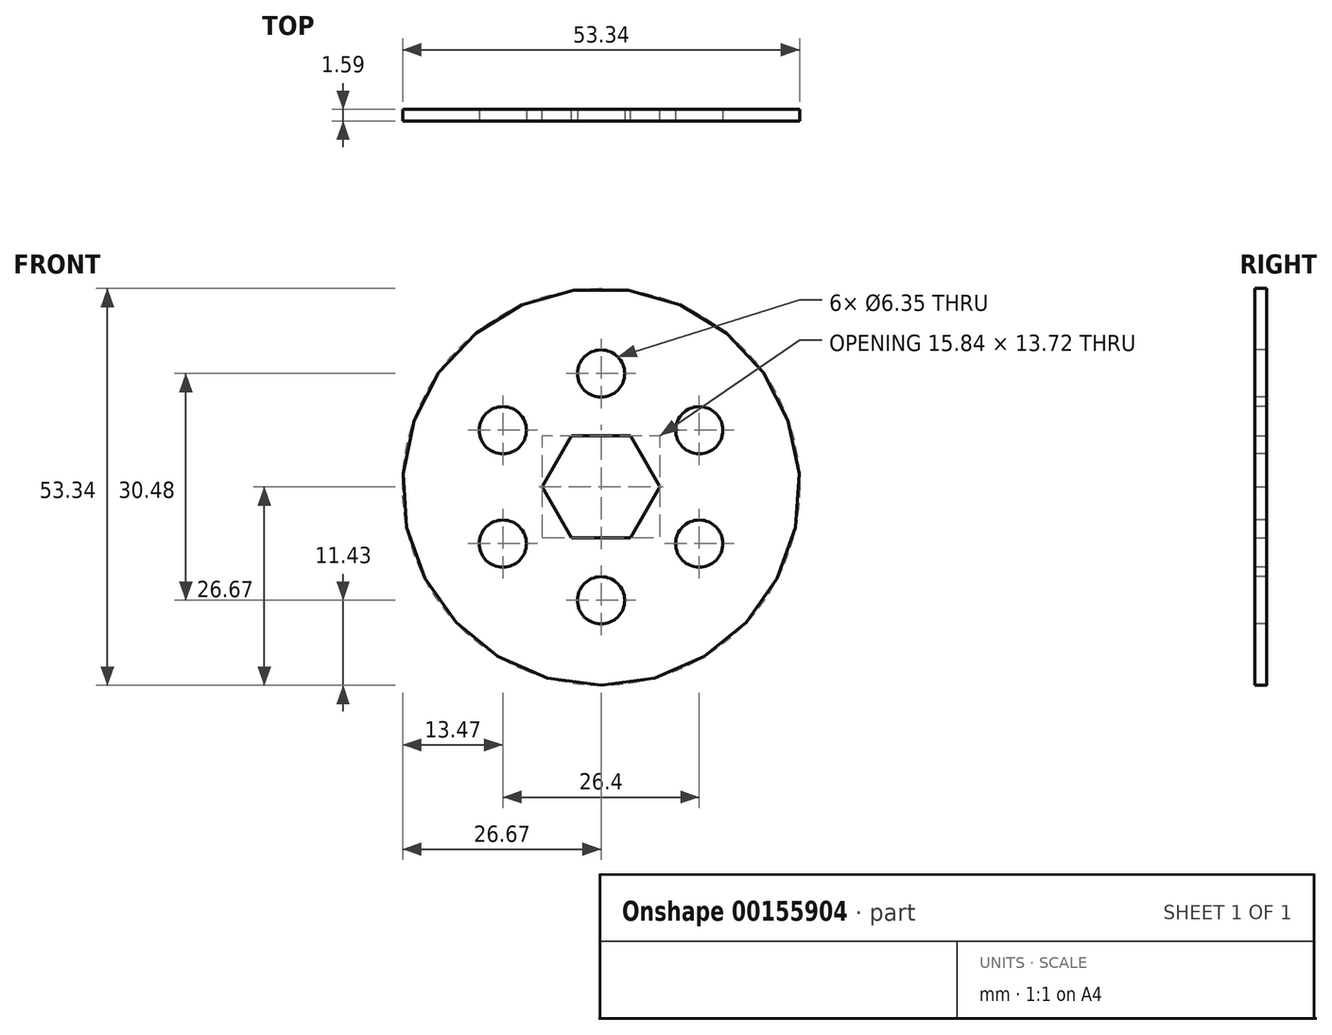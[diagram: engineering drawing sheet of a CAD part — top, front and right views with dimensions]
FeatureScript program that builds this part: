
annotation { "Feature Type Name" : "Feature", "Feature Type Description" : "" }
export const myFeature = defineFeature(function(context is Context, id is Id, definition is map)
    precondition{}
    {
        {
            var Q0;
            Q0=qCreatedBy(makeId("Front.planeOp"),FACE);
            var sketch = newSketch(context, id + "F0", { "sketchPlane" : qUnion([Q0])});
            skCircle(sketch, "E0", {"center": v(0, 0) * mm, "radius": 25.4 * mm});
            skCircle(sketch, "E1", {"center": v(0, 0) * mm, "radius": 7.92 * mm});
            skCircle(sketch, "E2", {"center": v(0, 0) * mm, "radius": 26.67 * mm});
            skCircle(sketch, "E3.cCircle", {"center": v(0, 0) * mm, "radius": 7.92 * mm, "construction": true});
            skLineSegment(sketch, "E3.0", {"start": v(3.96, 6.86) * mm, "end": v(7.92, 0) * mm});
            skLineSegment(sketch, "E3.1", {"start": v(7.92, 0) * mm, "end": v(3.96, -6.86) * mm});
            skLineSegment(sketch, "E3.2", {"start": v(3.96, -6.86) * mm, "end": v(-3.96, -6.86) * mm});
            skLineSegment(sketch, "E3.3", {"start": v(-3.96, -6.86) * mm, "end": v(-7.92, 0) * mm});
            skLineSegment(sketch, "E3.4", {"start": v(-7.92, 0) * mm, "end": v(-3.96, 6.86) * mm});
            skLineSegment(sketch, "E3.5", {"start": v(-3.96, 6.86) * mm, "end": v(3.96, 6.86) * mm});
            skSolve(sketch);
        }
        {
            var Q0;
            Q0 = qSketchRegion(id + "F0", true);
            var Q1;
            Q1=makeQuery(id+"F0.imprint","IMPRINT",FACE,{"disambiguationData":[TD([[makeQuery(id+"F0.imprint","IMPRINT",EDGE,{"derivedFrom":sQuery(id+"F0.wireOp",EDGE,"E0")}),1.0]])]});
            var Q2;
            Q2=makeQuery(id+"F0.imprint","IMPRINT",FACE,{"disambiguationData":[TD([[makeQuery(id+"F0.imprint","IMPRINT",EDGE,{"derivedFrom":sQuery(id+"F0.wireOp",EDGE,"E3.0")}),-1.0]])]});
            var Q3;
            {var subQ0=sQuery(id+"F0.wireOp",EDGE,"E3.5");Q3=makeQuery(id+"F0.imprint","IMPRINT",FACE,{"disambiguationData":[TD([[makeQuery(id+"F0.imprint","IMPRINT",EDGE,{"derivedFrom":subQ0}),1.0]])]});}
            var Q4;
            {var subQ0=sQuery(id+"F0.wireOp",EDGE,"E3.0");Q4=makeQuery(id+"F0.imprint","IMPRINT",FACE,{"disambiguationData":[TD([[makeQuery(id+"F0.imprint","IMPRINT",EDGE,{"derivedFrom":subQ0}),1.0]])]});}
            var Q5;
            {var subQ0=sQuery(id+"F0.wireOp",EDGE,"E3.1");Q5=makeQuery(id+"F0.imprint","IMPRINT",FACE,{"disambiguationData":[TD([[makeQuery(id+"F0.imprint","IMPRINT",EDGE,{"derivedFrom":subQ0}),1.0]])]});}
            var Q6;
            {var subQ0=sQuery(id+"F0.wireOp",EDGE,"E3.2");Q6=makeQuery(id+"F0.imprint","IMPRINT",FACE,{"disambiguationData":[TD([[makeQuery(id+"F0.imprint","IMPRINT",EDGE,{"derivedFrom":subQ0}),1.0]])]});}
            var Q7;
            {var subQ0=sQuery(id+"F0.wireOp",EDGE,"E3.3");Q7=makeQuery(id+"F0.imprint","IMPRINT",FACE,{"disambiguationData":[TD([[makeQuery(id+"F0.imprint","IMPRINT",EDGE,{"derivedFrom":subQ0}),1.0]])]});}
            var Q8;
            {var subQ0=sQuery(id+"F0.wireOp",EDGE,"E3.4");Q8=makeQuery(id+"F0.imprint","IMPRINT",FACE,{"disambiguationData":[TD([[makeQuery(id+"F0.imprint","IMPRINT",EDGE,{"derivedFrom":subQ0}),1.0]])]});}
            extrude(context, id + "F1", {"entities" : qUnion([Q0, Q1, Q2, Q3, Q4, Q5, Q6, Q7, Q8]), "depth" : 1 / 406.4 * mm});
        }
        {
            var Q0;
            Q0=makeQuery(id+"F1.opExtrude","CAP_FACE",FACE,{"disambiguationData":[OSD([sQuery(id+"F0.wireOp",EDGE,"E2")])],"isStart":false});
            var sketch = newSketch(context, id + "F2", { "sketchPlane" : qUnion([Q0])});
            skCircle(sketch, "E4.0", {"center": v(0, 0) * mm, "radius": 25.4 * mm});
            skCircle(sketch, "E5.0", {"center": v(0, 0) * mm, "radius": 7.92 * mm});
            skLineSegment(sketch, "E6.0", {"start": v(3.96, 6.86) * mm, "end": v(7.92, 0) * mm});
            skLineSegment(sketch, "E7.0", {"start": v(7.92, 0) * mm, "end": v(3.96, -6.86) * mm});
            skLineSegment(sketch, "E8.0", {"start": v(3.96, -6.86) * mm, "end": v(-3.96, -6.86) * mm});
            skLineSegment(sketch, "E9.0", {"start": v(-3.96, -6.86) * mm, "end": v(-7.92, 0) * mm});
            skLineSegment(sketch, "E10.0", {"start": v(-7.92, 0) * mm, "end": v(-3.96, 6.86) * mm});
            skLineSegment(sketch, "E11.0", {"start": v(-3.96, 6.86) * mm, "end": v(3.96, 6.86) * mm});
            skSolve(sketch);
        }
        {
            var Q0;
            Q0=makeQuery(id+"F2.imprint","IMPRINT",FACE,{"disambiguationData":[TD([[makeQuery(id+"F2.imprint","IMPRINT",EDGE,{"derivedFrom":sQuery(id+"F2.wireOp",EDGE,"E4.0")}),1.0]])]});
            var Q1;
            {var subQ0=sQuery(id+"F2.wireOp",EDGE,"E6.0");Q1=makeQuery(id+"F2.imprint","IMPRINT",FACE,{"disambiguationData":[TD([[makeQuery(id+"F2.imprint","IMPRINT",EDGE,{"derivedFrom":subQ0}),1.0]])]});}
            var Q2;
            {var subQ0=sQuery(id+"F2.wireOp",EDGE,"E11.0");Q2=makeQuery(id+"F2.imprint","IMPRINT",FACE,{"disambiguationData":[TD([[makeQuery(id+"F2.imprint","IMPRINT",EDGE,{"derivedFrom":subQ0}),1.0]])]});}
            var Q3;
            {var subQ0=sQuery(id+"F2.wireOp",EDGE,"E10.0");Q3=makeQuery(id+"F2.imprint","IMPRINT",FACE,{"disambiguationData":[TD([[makeQuery(id+"F2.imprint","IMPRINT",EDGE,{"derivedFrom":subQ0}),1.0]])]});}
            var Q4;
            {var subQ0=sQuery(id+"F2.wireOp",EDGE,"E9.0");Q4=makeQuery(id+"F2.imprint","IMPRINT",FACE,{"disambiguationData":[TD([[makeQuery(id+"F2.imprint","IMPRINT",EDGE,{"derivedFrom":subQ0}),1.0]])]});}
            var Q5;
            {var subQ0=sQuery(id+"F2.wireOp",EDGE,"E8.0");Q5=makeQuery(id+"F2.imprint","IMPRINT",FACE,{"disambiguationData":[TD([[makeQuery(id+"F2.imprint","IMPRINT",EDGE,{"derivedFrom":subQ0}),1.0]])]});}
            var Q6;
            {var subQ0=sQuery(id+"F2.wireOp",EDGE,"E7.0");Q6=makeQuery(id+"F2.imprint","IMPRINT",FACE,{"disambiguationData":[TD([[makeQuery(id+"F2.imprint","IMPRINT",EDGE,{"derivedFrom":subQ0}),1.0]])]});}
            extrude(context, id + "F3", {"entities" : qUnion([Q0, Q1, Q2, Q3, Q4, Q5, Q6]), "operationType" : NewBodyOperationType.ADD, "depth" : 1 / 406.4 * mm});
        }
        {
            var Q0;
            Q0=makeQuery(id+"F3.opExtrude","CAP_FACE",FACE,{"disambiguationData":[OSD([sQuery(id+"F2.wireOp",EDGE,"E4.0"),sQuery(id+"F2.wireOp",EDGE,"E6.0"),sQuery(id+"F2.wireOp",EDGE,"E7.0"),sQuery(id+"F2.wireOp",EDGE,"E8.0"),sQuery(id+"F2.wireOp",EDGE,"E9.0"),sQuery(id+"F2.wireOp",EDGE,"E10.0"),sQuery(id+"F2.wireOp",EDGE,"E11.0")])],"isStart":false});
            var sketch = newSketch(context, id + "F4", { "sketchPlane" : qUnion([Q0])});
            skCircle(sketch, "E12.0", {"center": v(0, 0) * mm, "radius": 26.67 * mm});
            skLineSegment(sketch, "E13.0", {"start": v(3.96, -6.86) * mm, "end": v(-3.96, -6.86) * mm});
            skLineSegment(sketch, "E14.0", {"start": v(7.92, 0) * mm, "end": v(3.96, -6.86) * mm});
            skLineSegment(sketch, "E15.0", {"start": v(3.96, 6.86) * mm, "end": v(7.92, 0) * mm});
            skLineSegment(sketch, "E16.0", {"start": v(-3.96, 6.86) * mm, "end": v(3.96, 6.86) * mm});
            skLineSegment(sketch, "E17.0", {"start": v(-7.92, 0) * mm, "end": v(-3.96, 6.86) * mm});
            skLineSegment(sketch, "E18.0", {"start": v(-3.96, -6.86) * mm, "end": v(-7.92, 0) * mm});
            skSolve(sketch);
        }
        {
            var Q0;
            Q0=makeQuery(id+"F4.imprint","IMPRINT",FACE,{"disambiguationData":[TD([[makeQuery(id+"F4.imprint","IMPRINT",EDGE,{"derivedFrom":sQuery(id+"F4.wireOp",EDGE,"E13.0")}),1.0]])]});
            var Q1;
            Q1=makeQuery(id+"F4.imprint","IMPRINT",FACE,{"disambiguationData":[TD([[makeQuery(id+"F4.imprint","IMPRINT",EDGE,{"derivedFrom":sQuery(id+"F4.wireOp",EDGE,"E12.0")}),1.0]])]});
            var Q2;
            Q2=makeQuery(id+"F0.imprint","IMPRINT",FACE,{"disambiguationData":[TD([[makeQuery(id+"F0.imprint","IMPRINT",EDGE,{"derivedFrom":sQuery(id+"F0.wireOp",EDGE,"E0")}),-1.0]])]});
            extrude(context, id + "F5", {"entities" : qUnion([Q0, Q1, Q2]), "operationType" : NewBodyOperationType.ADD, "depth" : 1.59 * mm});
        }
        {
            var Q0;
            Q0=makeQuery(id+"F3.boolean.opBoolean","SPLIT",FACE,{"disambiguationData":[TD([makeQuery(id+"F3.opExtrude","SWEPT_FACE",FACE,{"disambiguationData":[OSD([sQuery(id+"F2.wireOp",EDGE,"E6.0")])]})])],"derivedFrom":makeQuery(id+"F1.opExtrude","CAP_FACE",FACE,{"disambiguationData":[OSD([sQuery(id+"F0.wireOp",EDGE,"E2")])],"isStart":false})});
            var sketch = newSketch(context, id + "F6", { "sketchPlane" : qUnion([Q0])});
            skCircle(sketch, "E19", {"center": v(0, 0) * mm, "radius": 1.9 * mm});
            skSolve(sketch);
        }
        {
            var Q0;
            Q0 = qSketchRegion(id + "F6", true);
            extrude(context, id + "F7", {"entities" : qUnion([Q0]), "operationType" : NewBodyOperationType.REMOVE, "oppositeDirection" : true, "depth" : 25.4 * mm});
        }
        {
            var Q0;
            Q0=makeQuery(id+"F5.opExtrude","CAP_FACE",FACE,{"disambiguationData":[OSD([sQuery(id+"F4.wireOp",EDGE,"E12.0"),sQuery(id+"F4.wireOp",EDGE,"E13.0"),sQuery(id+"F4.wireOp",EDGE,"E14.0"),sQuery(id+"F4.wireOp",EDGE,"E15.0"),sQuery(id+"F4.wireOp",EDGE,"E16.0"),sQuery(id+"F4.wireOp",EDGE,"E17.0"),sQuery(id+"F4.wireOp",EDGE,"E18.0")])],"isStart":false});
            var sketch = newSketch(context, id + "F8", { "sketchPlane" : qUnion([Q0])});
            skPoint(sketch, "E20", {"position": v(0, 15.24) * mm});
            skPoint(sketch, "E21.1.0", {"position": v(-13.2, 7.62) * mm});
            skPoint(sketch, "E21.2.0", {"position": v(-13.2, -7.62) * mm});
            skPoint(sketch, "E21.3.0", {"position": v(0, -15.24) * mm});
            skPoint(sketch, "E21.4.0", {"position": v(13.2, -7.62) * mm});
            skPoint(sketch, "E21.5.0", {"position": v(13.2, 7.62) * mm});
            skPoint(sketch, "E21.center", {"position": v(0, 0) * mm});
            skSolve(sketch);
        }
        {
            var Q0;
            Q0=sQuery(id+"F8.wireOp",VERTEX,"E20");
            var Q1;
            Q1=sQuery(id+"F8.wireOp",VERTEX,"E21.3.0");
            var Q2;
            Q2=sQuery(id+"F8.wireOp",VERTEX,"E21.2.0");
            var Q3;
            Q3=sQuery(id+"F8.wireOp",VERTEX,"E21.1.0");
            var Q4;
            Q4=sQuery(id+"F8.wireOp",VERTEX,"E21.5.0");
            var Q5;
            Q5=sQuery(id+"F8.wireOp",VERTEX,"E21.4.0");
            var Q6;
            Q6=makeQuery(id+"F1.opExtrude","SWEPT_BODY",BODY,{"disambiguationData":[OSD([sQuery(id+"F0.wireOp",EDGE,"E2")])]});
            hole(context, id + "F9", {"style" : HoleStyle.SIMPLE, "endStyle" : HoleEndStyle.THROUGH, "holeDiameter" : 6.35 * mm, "locations" : qUnion([Q0, Q1, Q2, Q3, Q4, Q5]), "scope" : qUnion([Q6]), "isTappedThrough" : true});
        }
    });
